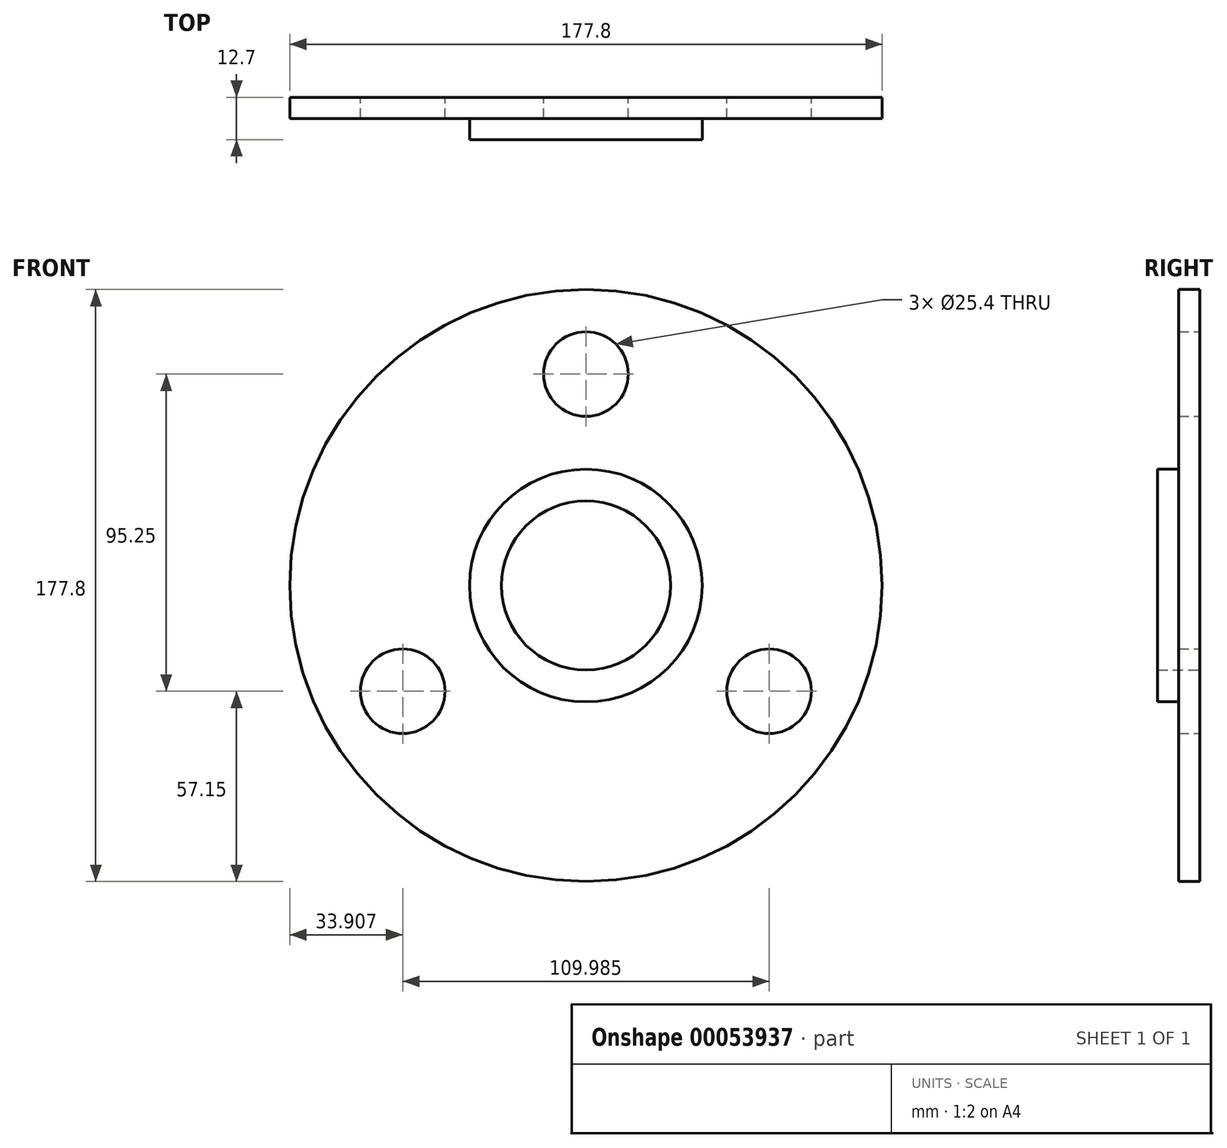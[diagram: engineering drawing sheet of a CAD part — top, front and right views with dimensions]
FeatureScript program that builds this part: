
annotation { "Feature Type Name" : "Feature", "Feature Type Description" : "" }
export const myFeature = defineFeature(function(context is Context, id is Id, definition is map)
    precondition{}
    {
        {
            var Q0;
            Q0=qCreatedBy(makeId("Front.planeOp"),FACE);
            var sketch = newSketch(context, id + "F0", { "sketchPlane" : qUnion([Q0])});
            skCircle(sketch, "E0", {"center": v(0, 0) * mm, "radius": 88.9 * mm});
            skCircle(sketch, "E1", {"center": v(0, 0) * mm, "radius": 25.4 * mm});
            skCircle(sketch, "E2", {"center": v(0, 0) * mm, "radius": 63.5 * mm, "construction": true});
            skCircle(sketch, "E3", {"center": v(0, 63.5) * mm, "radius": 12.7 * mm});
            skCircle(sketch, "E4.1.0", {"center": v(-55, -31.75) * mm, "radius": 12.7 * mm});
            skCircle(sketch, "E4.2.0", {"center": v(55, -31.75) * mm, "radius": 12.7 * mm});
            skCircle(sketch, "E5", {"center": v(0, 0) * mm, "radius": 34.93 * mm});
            skSolve(sketch);
        }
        {
            var Q0;
            Q0=makeQuery(id+"F0.imprint","IMPRINT",FACE,{"disambiguationData":[TD([[makeQuery(id+"F0.imprint","IMPRINT",EDGE,{"derivedFrom":sQuery(id+"F0.wireOp",EDGE,"E0")}),1.0]])]});
            extrude(context, id + "F1", {"entities" : qUnion([Q0]), "depth" : 6.35 * mm});
        }
        {
            var Q0;
            Q0=makeQuery(id+"F0.imprint","IMPRINT",FACE,{"disambiguationData":[TD([[makeQuery(id+"F0.imprint","IMPRINT",EDGE,{"derivedFrom":sQuery(id+"F0.wireOp",EDGE,"E1")}),-1.0]])]});
            extrude(context, id + "F2", {"entities" : qUnion([Q0]), "operationType" : NewBodyOperationType.ADD, "depth" : 12.7 * mm});
        }
    });
